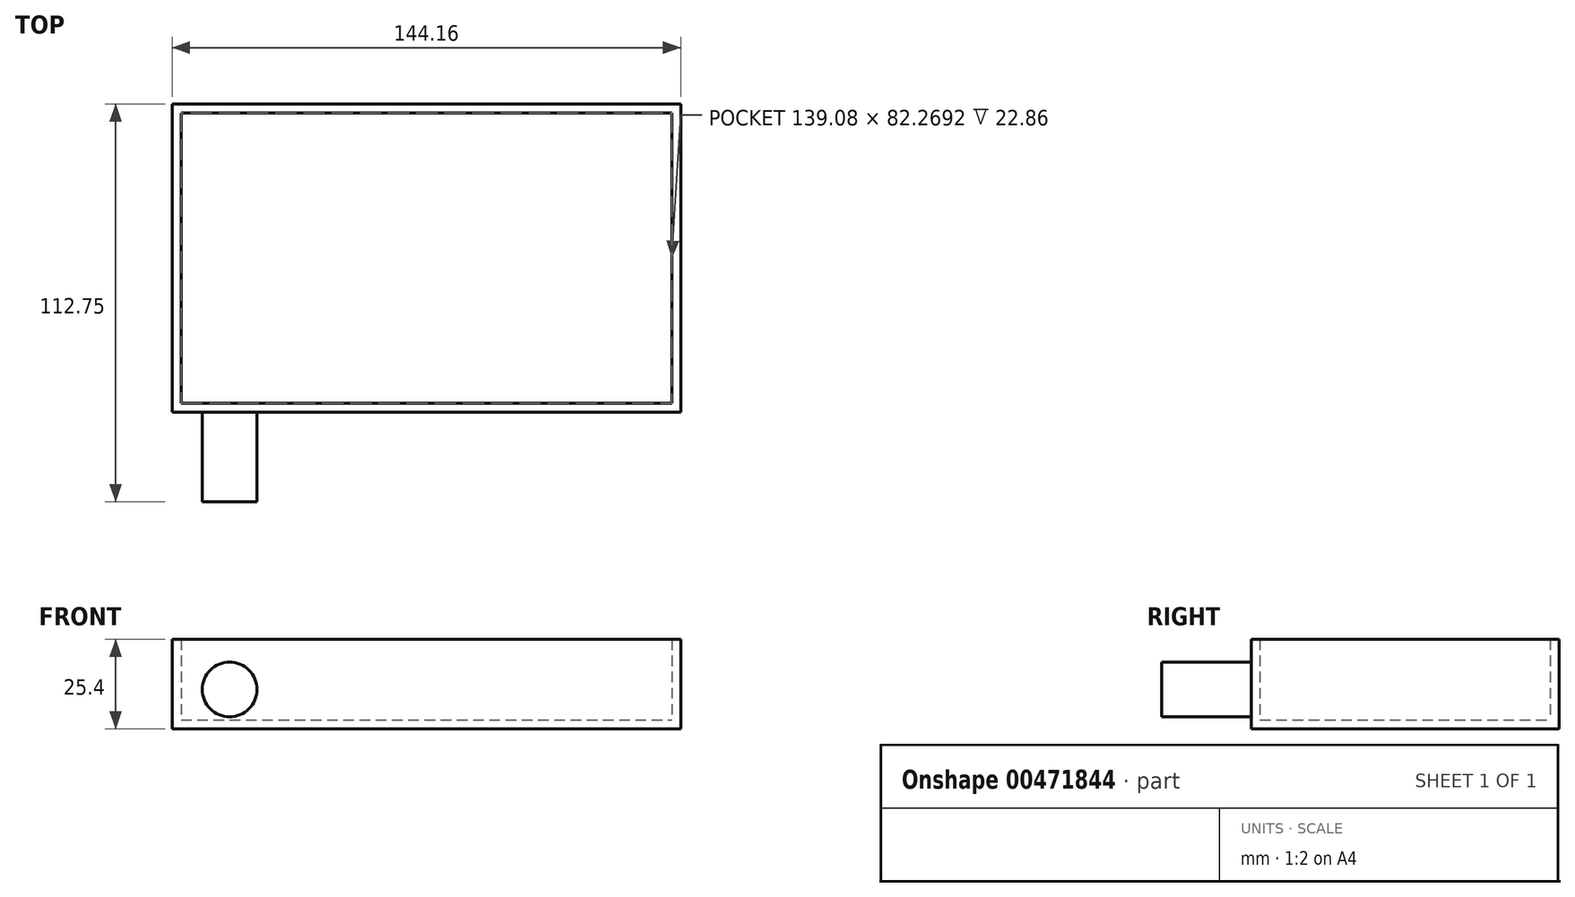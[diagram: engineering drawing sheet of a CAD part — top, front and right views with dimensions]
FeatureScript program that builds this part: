
annotation { "Feature Type Name" : "Feature", "Feature Type Description" : "" }
export const myFeature = defineFeature(function(context is Context, id is Id, definition is map)
    precondition{}
    {
        {
            var Q0;
            Q0=qCreatedBy(makeId("Top.planeOp"),FACE);
            var sketch = newSketch(context, id + "F0", { "sketchPlane" : qUnion([Q0])});
            skLineSegment(sketch, "E0.bottom", {"start": v(-62.36, -65.86) * mm, "end": v(81.8, -65.86) * mm});
            skLineSegment(sketch, "E0.top", {"start": v(-62.36, 21.49) * mm, "end": v(81.8, 21.49) * mm});
            skLineSegment(sketch, "E0.left", {"start": v(-62.36, -65.86) * mm, "end": v(-62.36, 21.49) * mm});
            skLineSegment(sketch, "E0.right", {"start": v(81.8, -65.86) * mm, "end": v(81.8, 21.49) * mm});
            skSolve(sketch);
        }
        {
            var Q0;
            Q0=makeQuery(id+"F0.imprint","IMPRINT",FACE,{"disambiguationData":[TD([[makeQuery(id+"F0.imprint","IMPRINT",EDGE,{"derivedFrom":sQuery(id+"F0.wireOp",EDGE,"E0.bottom")}),1.0]])]});
            extrude(context, id + "F1", {"entities" : qUnion([Q0]), "depth" : 25.4 * mm});
        }
        {
            var Q0;
            Q0=makeQuery(id+"F1.opExtrude","CAP_FACE",FACE,{"disambiguationData":[OSD([sQuery(id+"F0.wireOp",EDGE,"E0.bottom"),sQuery(id+"F0.wireOp",EDGE,"E0.top"),sQuery(id+"F0.wireOp",EDGE,"E0.left"),sQuery(id+"F0.wireOp",EDGE,"E0.right")])],"isStart":false});
            shell(context, id + "F2", {"entities" : qUnion([Q0]), "thickness" : 2.54 * mm});
        }
        {
            var Q0;
            Q0=makeQuery(id+"F1.opExtrude","SWEPT_FACE",FACE,{"disambiguationData":[OSD([sQuery(id+"F0.wireOp",EDGE,"E0.bottom")])]});
            var sketch = newSketch(context, id + "F3", { "sketchPlane" : qUnion([Q0])});
            skCircle(sketch, "E1", {"center": v(-46.06, 11.17) * mm, "radius": 7.77 * mm});
            skSolve(sketch);
        }
        {
            var Q0;
            Q0=makeQuery(id+"F3.imprint","IMPRINT",FACE,{"disambiguationData":[TD([[makeQuery(id+"F3.imprint","IMPRINT",EDGE,{"derivedFrom":sQuery(id+"F3.wireOp",EDGE,"E1")}),1.0]])]});
            extrude(context, id + "F4", {"entities" : qUnion([Q0]), "operationType" : NewBodyOperationType.ADD, "depth" : 25.4 * mm});
        }
    });
